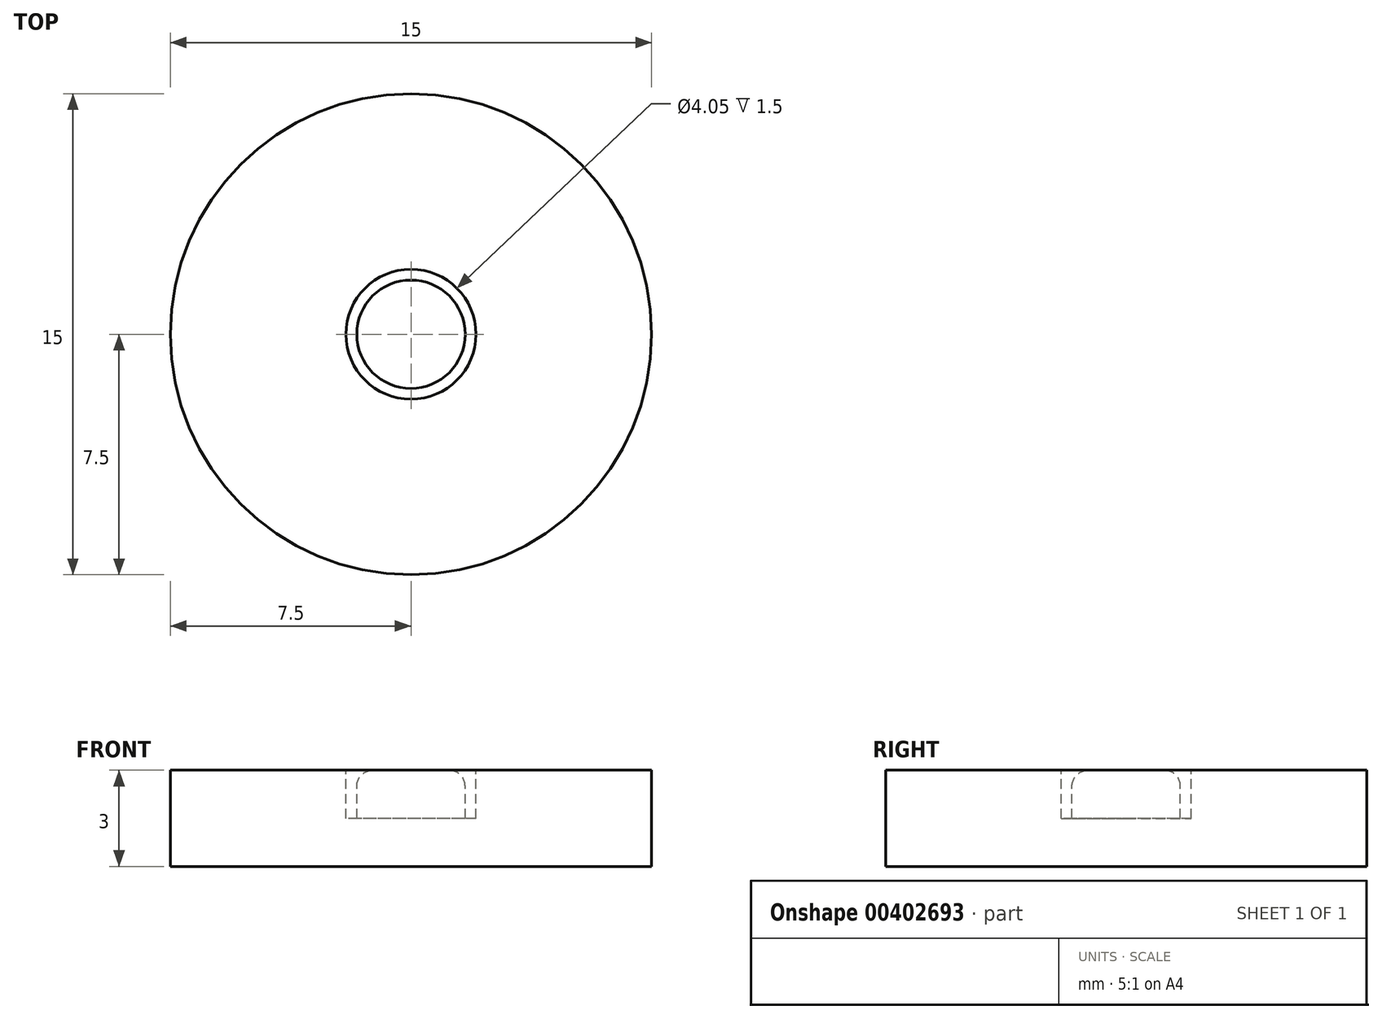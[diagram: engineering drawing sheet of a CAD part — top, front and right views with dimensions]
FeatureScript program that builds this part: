
annotation { "Feature Type Name" : "Feature", "Feature Type Description" : "" }
export const myFeature = defineFeature(function(context is Context, id is Id, definition is map)
    precondition{}
    {
        {
            var Q0;
            Q0=qCreatedBy(makeId("Top.planeOp"),FACE);
            var sketch = newSketch(context, id + "F0", { "sketchPlane" : qUnion([Q0])});
            skCircle(sketch, "E0", {"center": v(0, 0) * mm, "radius": 7.5 * mm});
            skCircle(sketch, "E1", {"center": v(0, 0) * mm, "radius": 1.69 * mm});
            skCircle(sketch, "E2", {"center": v(0, 0) * mm, "radius": 2.03 * mm});
            skSolve(sketch);
        }
        {
            var Q0;
            Q0=makeQuery(id+"F0.imprint","IMPRINT",FACE,{"disambiguationData":[TD([[makeQuery(id+"F0.imprint","IMPRINT",EDGE,{"derivedFrom":sQuery(id+"F0.wireOp",EDGE,"E1")}),1.0]])]});
            var Q1;
            Q1=makeQuery(id+"F0.imprint","IMPRINT",FACE,{"disambiguationData":[TD([[makeQuery(id+"F0.imprint","IMPRINT",EDGE,{"derivedFrom":sQuery(id+"F0.wireOp",EDGE,"E0")}),1.0]])]});
            var Q2;
            Q2=makeQuery(id+"F0.imprint","IMPRINT",FACE,{"disambiguationData":[TD([[makeQuery(id+"F0.imprint","IMPRINT",EDGE,{"derivedFrom":sQuery(id+"F0.wireOp",EDGE,"E1")}),-1.0]])]});
            extrude(context, id + "F1", {"entities" : qUnion([Q0, Q1, Q2]), "depth" : 3 * mm});
        }
        {
            var Q0;
            Q0=makeQuery(id+"F1.opExtrude","CAP_FACE",FACE,{"disambiguationData":[OSD([sQuery(id+"F0.wireOp",EDGE,"E0")])],"isStart":false});
            var sketch = newSketch(context, id + "F2", { "sketchPlane" : qUnion([Q0])});
            skCircle(sketch, "E3", {"center": v(0, 0) * mm, "radius": 7.5 * mm});
            skCircle(sketch, "E4", {"center": v(0, 0) * mm, "radius": 1.69 * mm});
            skCircle(sketch, "E5", {"center": v(0, 0) * mm, "radius": 2.03 * mm});
            skSolve(sketch);
        }
        {
            var Q0;
            Q0=makeQuery(id+"F2.imprint","IMPRINT",FACE,{"disambiguationData":[TD([[makeQuery(id+"F2.imprint","IMPRINT",EDGE,{"derivedFrom":sQuery(id+"F2.wireOp",EDGE,"E4")}),-1.0]])]});
            var Q1;
            Q1=sQuery(id+"F2.wireOp",EDGE,"E3");
            var Q2;
            Q2=sQuery(id+"F2.wireOp",EDGE,"E4");
            var Q3;
            Q3=sQuery(id+"F2.wireOp",EDGE,"E5");
            extrude(context, id + "F3", {"entities" : qUnion([Q0]), "operationType" : NewBodyOperationType.REMOVE, "surfaceEntities" : qUnion([Q1, Q2, Q3]), "oppositeDirection" : true, "depth" : 1.5 * mm});
        }
        {
            var Q0;
            Q0=makeQuery(id+"F3.boolean.opBoolean","COPY",EDGE,{"derivedFrom":makeQuery(id+"F3.opExtrude","CAP_EDGE",EDGE,{"disambiguationData":[OSD([sQuery(id+"F2.wireOp",EDGE,"E4")])],"isStart":true})});
            var Q1;
            Q1=makeQuery(id+"F3.boolean.opBoolean","COPY",EDGE,{"derivedFrom":makeQuery(id+"F3.opExtrude","CAP_EDGE",EDGE,{"disambiguationData":[OSD([sQuery(id+"F2.wireOp",EDGE,"E5")])],"isStart":true})});
            fillet(context, id + "F4", {"entities" : qUnion([Q0, Q1]), "radius" : 0.5 * mm, "tangentPropagation" : true, "allowEdgeOverflow" : false});
        }
    });
